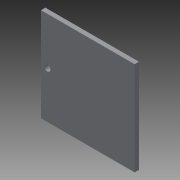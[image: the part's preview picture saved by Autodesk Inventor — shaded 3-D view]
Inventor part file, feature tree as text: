
AUTODESK INVENTOR PART (.ipt)
format: ipt  version: 2015 (Build 190159000, 159)  size: 98,304 bytes
history: native  units: mm
features: extrude x3, sketch x3, projected_geometry x2
ambient origin geometry x8: Origin, YZ Plane, XZ Plane, XY Plane, X Axis, Y Axis, Z Axis, Center Point
bodies: Solid1 (feature_tree)
feature tree (8):
  extrude  "Extrusion1"  Depth=75.0mm
  extrude  "Extrusion2"  Depth=3.5mm
  extrude  "Extrusion3"  Depth=32.0mm
  sketch  "Sketch1"  dims[d0=75.0mm d1=75.0mm]
  sketch  "Sketch2"  dims[d2=3.5mm d3=0.0mm d4=5.0mm]
  projected_geometry  "Projected Loop1"
  sketch  "Sketch3"  dims[d5=5.0mm d6=5.0mm d7=5.0mm d8=3.5mm d9=0.0mm d10=10.0mm d11=32.0mm d12=0.0mm]
  projected_geometry  "Projected Loop2"
